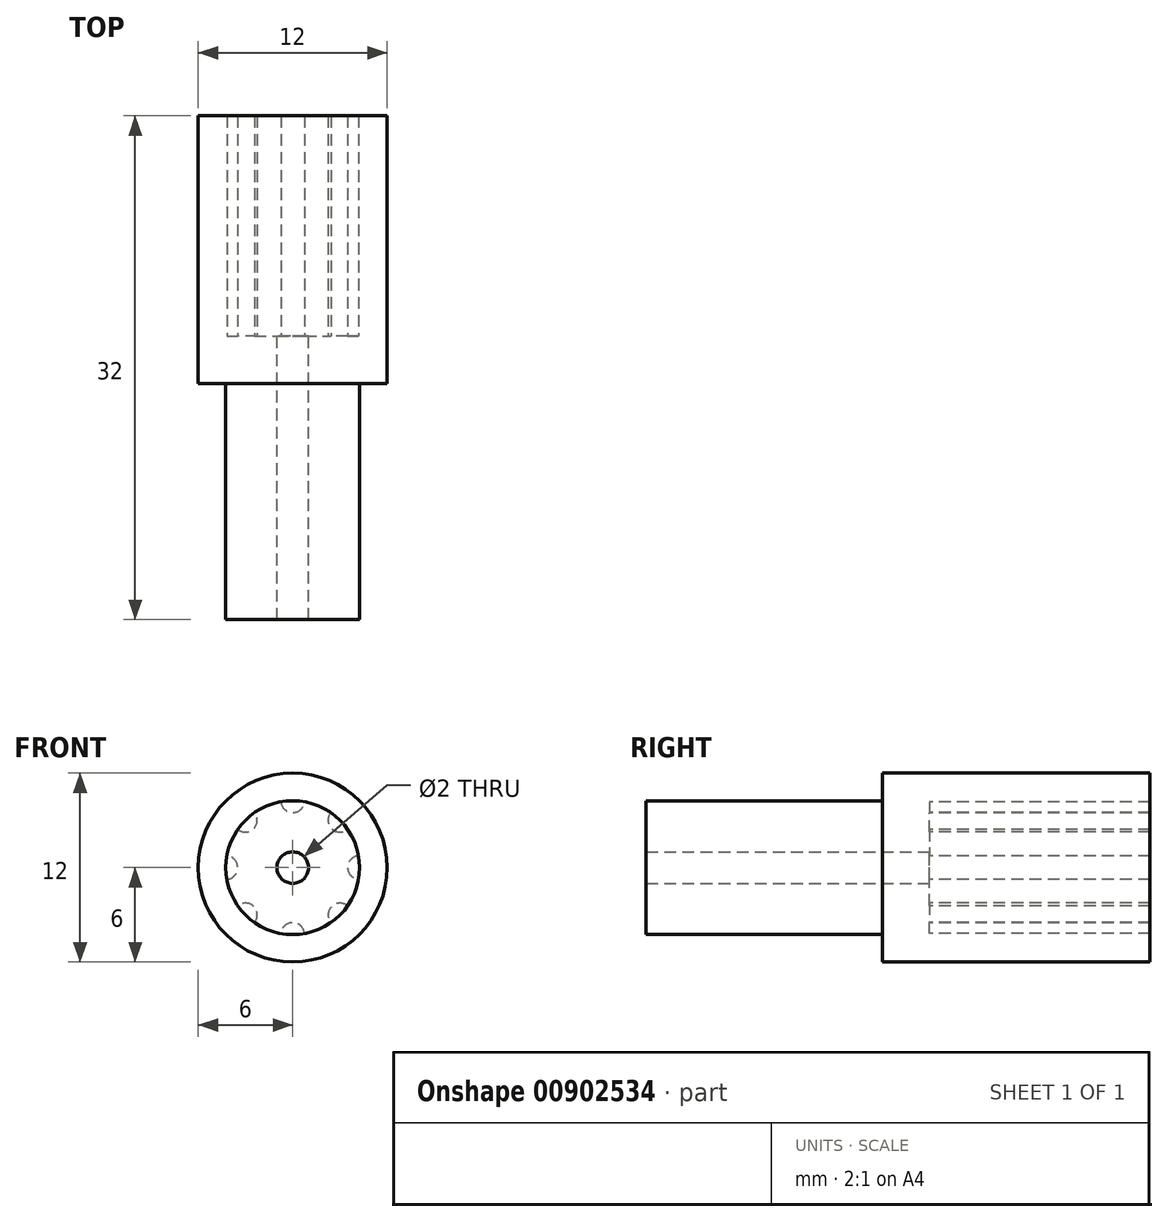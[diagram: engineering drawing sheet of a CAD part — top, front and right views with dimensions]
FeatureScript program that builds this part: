
annotation { "Feature Type Name" : "Feature", "Feature Type Description" : "" }
export const myFeature = defineFeature(function(context is Context, id is Id, definition is map)
    precondition{}
    {
        {
            var Q0;
            Q0=qCreatedBy(makeId("Front.planeOp"),FACE);
            var sketch = newSketch(context, id + "F0", { "sketchPlane" : qUnion([Q0])});
            skCircle(sketch, "E0", {"center": v(0, 0) * mm, "radius": 1 * mm});
            skCircle(sketch, "E1", {"center": v(0, 0) * mm, "radius": 2.5 * mm});
            skCircle(sketch, "E2", {"center": v(0, 0) * mm, "radius": 4.25 * mm});
            skCircle(sketch, "E3", {"center": v(0, 0) * mm, "radius": 6 * mm});
            skArc(sketch, "E4", {"start": v(-0.75, 4.18) * mm, "mid": v(0, 3.5) * mm, "end": v(0.75, 4.18) * mm});
            skArc(sketch, "E5.1.0", {"start": v(-3.49, 2.43) * mm, "mid": v(-2.47, 2.47) * mm, "end": v(-2.43, 3.49) * mm});
            skArc(sketch, "E5.2.0", {"start": v(-4.18, -0.75) * mm, "mid": v(-3.5, 0) * mm, "end": v(-4.18, 0.75) * mm});
            skArc(sketch, "E5.3.0", {"start": v(-2.43, -3.49) * mm, "mid": v(-2.47, -2.47) * mm, "end": v(-3.49, -2.43) * mm});
            skArc(sketch, "E5.4.0", {"start": v(0.75, -4.18) * mm, "mid": v(0, -3.5) * mm, "end": v(-0.75, -4.18) * mm});
            skArc(sketch, "E5.5.0", {"start": v(3.49, -2.43) * mm, "mid": v(2.47, -2.47) * mm, "end": v(2.43, -3.49) * mm});
            skArc(sketch, "E5.6.0", {"start": v(4.18, 0.75) * mm, "mid": v(3.5, 0) * mm, "end": v(4.18, -0.75) * mm});
            skArc(sketch, "E5.7.0", {"start": v(2.43, 3.49) * mm, "mid": v(2.47, 2.47) * mm, "end": v(3.49, 2.43) * mm});
            skSolve(sketch);
        }
        {
            var Q0;
            Q0=makeQuery(id+"F0.imprint","IMPRINT",FACE,{"disambiguationData":[TD([[makeQuery(id+"F0.imprint","IMPRINT",EDGE,{"derivedFrom":sQuery(id+"F0.wireOp",EDGE,"E3")}),1.0]])]});
            var Q1;
            {var subQ0=sQuery(id+"F0.wireOp",EDGE,"E5.6.0");Q1=makeQuery(id+"F0.imprint","IMPRINT",FACE,{"disambiguationData":[TD([[makeQuery(id+"F0.imprint","IMPRINT",EDGE,{"derivedFrom":subQ0}),1.0]])]});}
            var Q2;
            {var subQ0=sQuery(id+"F0.wireOp",EDGE,"E5.7.0");Q2=makeQuery(id+"F0.imprint","IMPRINT",FACE,{"disambiguationData":[TD([[makeQuery(id+"F0.imprint","IMPRINT",EDGE,{"derivedFrom":subQ0}),1.0]])]});}
            var Q3;
            {var subQ0=sQuery(id+"F0.wireOp",EDGE,"E4");Q3=makeQuery(id+"F0.imprint","IMPRINT",FACE,{"disambiguationData":[TD([[makeQuery(id+"F0.imprint","IMPRINT",EDGE,{"derivedFrom":subQ0}),1.0]])]});}
            var Q4;
            {var subQ0=sQuery(id+"F0.wireOp",EDGE,"E5.1.0");Q4=makeQuery(id+"F0.imprint","IMPRINT",FACE,{"disambiguationData":[TD([[makeQuery(id+"F0.imprint","IMPRINT",EDGE,{"derivedFrom":subQ0}),1.0]])]});}
            var Q5;
            {var subQ0=sQuery(id+"F0.wireOp",EDGE,"E5.2.0");Q5=makeQuery(id+"F0.imprint","IMPRINT",FACE,{"disambiguationData":[TD([[makeQuery(id+"F0.imprint","IMPRINT",EDGE,{"derivedFrom":subQ0}),1.0]])]});}
            var Q6;
            {var subQ0=sQuery(id+"F0.wireOp",EDGE,"E5.3.0");Q6=makeQuery(id+"F0.imprint","IMPRINT",FACE,{"disambiguationData":[TD([[makeQuery(id+"F0.imprint","IMPRINT",EDGE,{"derivedFrom":subQ0}),1.0]])]});}
            var Q7;
            {var subQ0=sQuery(id+"F0.wireOp",EDGE,"E5.4.0");Q7=makeQuery(id+"F0.imprint","IMPRINT",FACE,{"disambiguationData":[TD([[makeQuery(id+"F0.imprint","IMPRINT",EDGE,{"derivedFrom":subQ0}),1.0]])]});}
            var Q8;
            {var subQ0=sQuery(id+"F0.wireOp",EDGE,"E5.5.0");Q8=makeQuery(id+"F0.imprint","IMPRINT",FACE,{"disambiguationData":[TD([[makeQuery(id+"F0.imprint","IMPRINT",EDGE,{"derivedFrom":subQ0}),1.0]])]});}
            extrude(context, id + "F1", {"entities" : qUnion([Q0, Q1, Q2, Q3, Q4, Q5, Q6, Q7, Q8]), "oppositeDirection" : true, "depth" : 17 * mm, "offsetDistance" : 25 * mm});
        }
        {
            var Q0;
            Q0=makeQuery(id+"F0.imprint","IMPRINT",FACE,{"disambiguationData":[TD([[makeQuery(id+"F0.imprint","IMPRINT",EDGE,{"derivedFrom":sQuery(id+"F0.wireOp",EDGE,"E1")}),-1.0]])]});
            var Q1;
            Q1=makeQuery(id+"F0.imprint","IMPRINT",FACE,{"disambiguationData":[TD([[makeQuery(id+"F0.imprint","IMPRINT",EDGE,{"derivedFrom":sQuery(id+"F0.wireOp",EDGE,"E0")}),-1.0]])]});
            var Q2;
            {var subQ0=sQuery(id+"F0.wireOp",EDGE,"E5.1.0");Q2=makeQuery(id+"F0.imprint","IMPRINT",FACE,{"disambiguationData":[TD([[makeQuery(id+"F0.imprint","IMPRINT",EDGE,{"derivedFrom":subQ0}),1.0]])]});}
            var Q3;
            {var subQ0=sQuery(id+"F0.wireOp",EDGE,"E5.2.0");Q3=makeQuery(id+"F0.imprint","IMPRINT",FACE,{"disambiguationData":[TD([[makeQuery(id+"F0.imprint","IMPRINT",EDGE,{"derivedFrom":subQ0}),1.0]])]});}
            var Q4;
            {var subQ0=sQuery(id+"F0.wireOp",EDGE,"E5.3.0");Q4=makeQuery(id+"F0.imprint","IMPRINT",FACE,{"disambiguationData":[TD([[makeQuery(id+"F0.imprint","IMPRINT",EDGE,{"derivedFrom":subQ0}),1.0]])]});}
            var Q5;
            {var subQ0=sQuery(id+"F0.wireOp",EDGE,"E5.4.0");Q5=makeQuery(id+"F0.imprint","IMPRINT",FACE,{"disambiguationData":[TD([[makeQuery(id+"F0.imprint","IMPRINT",EDGE,{"derivedFrom":subQ0}),1.0]])]});}
            var Q6;
            {var subQ0=sQuery(id+"F0.wireOp",EDGE,"E5.5.0");Q6=makeQuery(id+"F0.imprint","IMPRINT",FACE,{"disambiguationData":[TD([[makeQuery(id+"F0.imprint","IMPRINT",EDGE,{"derivedFrom":subQ0}),1.0]])]});}
            var Q7;
            {var subQ0=sQuery(id+"F0.wireOp",EDGE,"E5.7.0");Q7=makeQuery(id+"F0.imprint","IMPRINT",FACE,{"disambiguationData":[TD([[makeQuery(id+"F0.imprint","IMPRINT",EDGE,{"derivedFrom":subQ0}),1.0]])]});}
            var Q8;
            {var subQ0=sQuery(id+"F0.wireOp",EDGE,"E4");Q8=makeQuery(id+"F0.imprint","IMPRINT",FACE,{"disambiguationData":[TD([[makeQuery(id+"F0.imprint","IMPRINT",EDGE,{"derivedFrom":subQ0}),1.0]])]});}
            var Q9;
            {var subQ0=sQuery(id+"F0.wireOp",EDGE,"E5.6.0");Q9=makeQuery(id+"F0.imprint","IMPRINT",FACE,{"disambiguationData":[TD([[makeQuery(id+"F0.imprint","IMPRINT",EDGE,{"derivedFrom":subQ0}),1.0]])]});}
            extrude(context, id + "F2", {"entities" : qUnion([Q0, Q1, Q2, Q3, Q4, Q5, Q6, Q7, Q8, Q9]), "operationType" : NewBodyOperationType.ADD, "depth" : 15 * mm, "offsetDistance" : 25 * mm, "hasSecondDirection" : true, "secondDirectionOppositeDirection" : true, "secondDirectionDepth" : 3 * mm});
        }
    });
